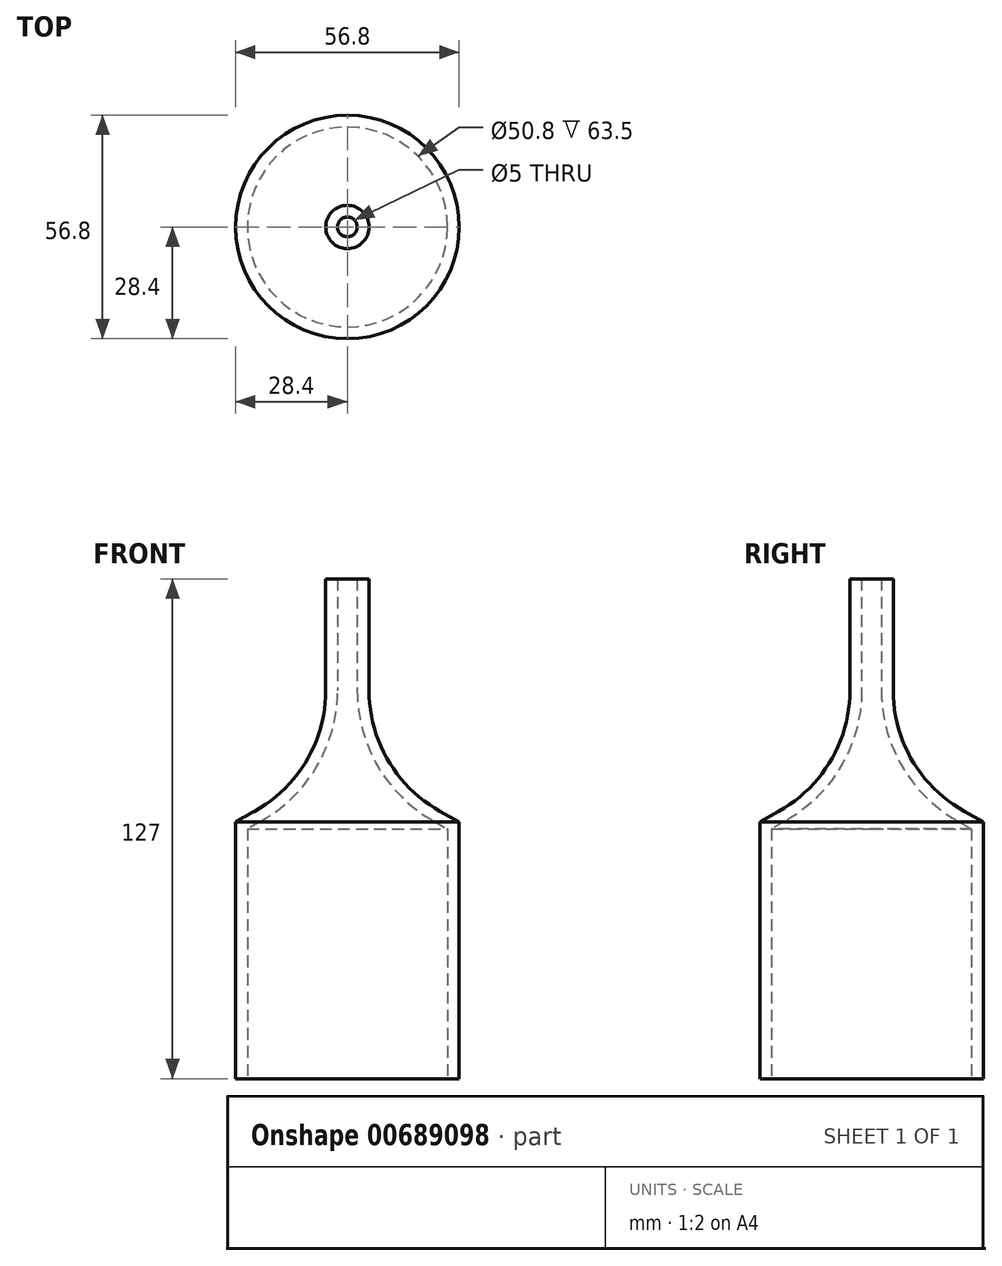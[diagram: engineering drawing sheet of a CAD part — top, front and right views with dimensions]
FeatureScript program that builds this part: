
annotation { "Feature Type Name" : "Feature", "Feature Type Description" : "" }
export const myFeature = defineFeature(function(context is Context, id is Id, definition is map)
    precondition{}
    {
        {
            var Q0;
            Q0=qCreatedBy(makeId("Front.planeOp"),FACE);
            var sketch = newSketch(context, id + "F0", { "sketchPlane" : qUnion([Q0])});
            skLineSegment(sketch, "E0", {"start": v(-25.4, 0) * mm, "end": v(-25.4, 63.5) * mm});
            skLineSegment(sketch, "E1", {"start": v(-25.4, 63.5) * mm, "end": v(-22.12, 65.32) * mm});
            skLineSegment(sketch, "E2", {"start": v(-2.5, 98.64) * mm, "end": v(-2.5, 127) * mm});
            skPoint(sketch, "E3.visualSharp", {"position": v(-2.5, 76.2) * mm});
            skArc(sketch, "E3.filletArc", {"start": v(-22.12, 65.32) * mm, "mid": v(-7.77, 79.3) * mm, "end": v(-2.5, 98.64) * mm});
            skLineSegment(sketch, "E4.0", {"start": v(-5.5, 98.64) * mm, "end": v(-5.5, 127) * mm});
            skArc(sketch, "E4.1", {"start": v(-23.58, 67.94) * mm, "mid": v(-10.35, 80.83) * mm, "end": v(-5.5, 98.64) * mm});
            skLineSegment(sketch, "E4.2", {"start": v(-28.4, 65.27) * mm, "end": v(-23.58, 67.94) * mm});
            skLineSegment(sketch, "E4.3", {"start": v(-28.4, 0) * mm, "end": v(-28.4, 65.27) * mm});
            skLineSegment(sketch, "E5", {"start": v(-28.4, 0) * mm, "end": v(-25.4, 0) * mm});
            skLineSegment(sketch, "E6", {"start": v(-5.5, 127) * mm, "end": v(-2.5, 127) * mm});
            skSolve(sketch);
        }
        {
            var Q0;
            Q0=qCreatedBy(makeId("Front.planeOp"),FACE);
            var sketch = newSketch(context, id + "F1", { "sketchPlane" : qUnion([Q0])});
            skLineSegment(sketch, "E7", {"start": v(0, 0) * mm, "end": v(0, 129.7) * mm});
            skSolve(sketch);
        }
        {
            var Q0;
            Q0 = qSketchRegion(id + "F0", true);
            var Q1;
            Q1=sQuery(id+"F1.wireOp",EDGE,"E7");
            revolve(context, id + "F2", {"entities" : qUnion([Q0]), "axis" : qUnion([Q1]), "revolveType" : RevolveType.FULL});
        }
    });
